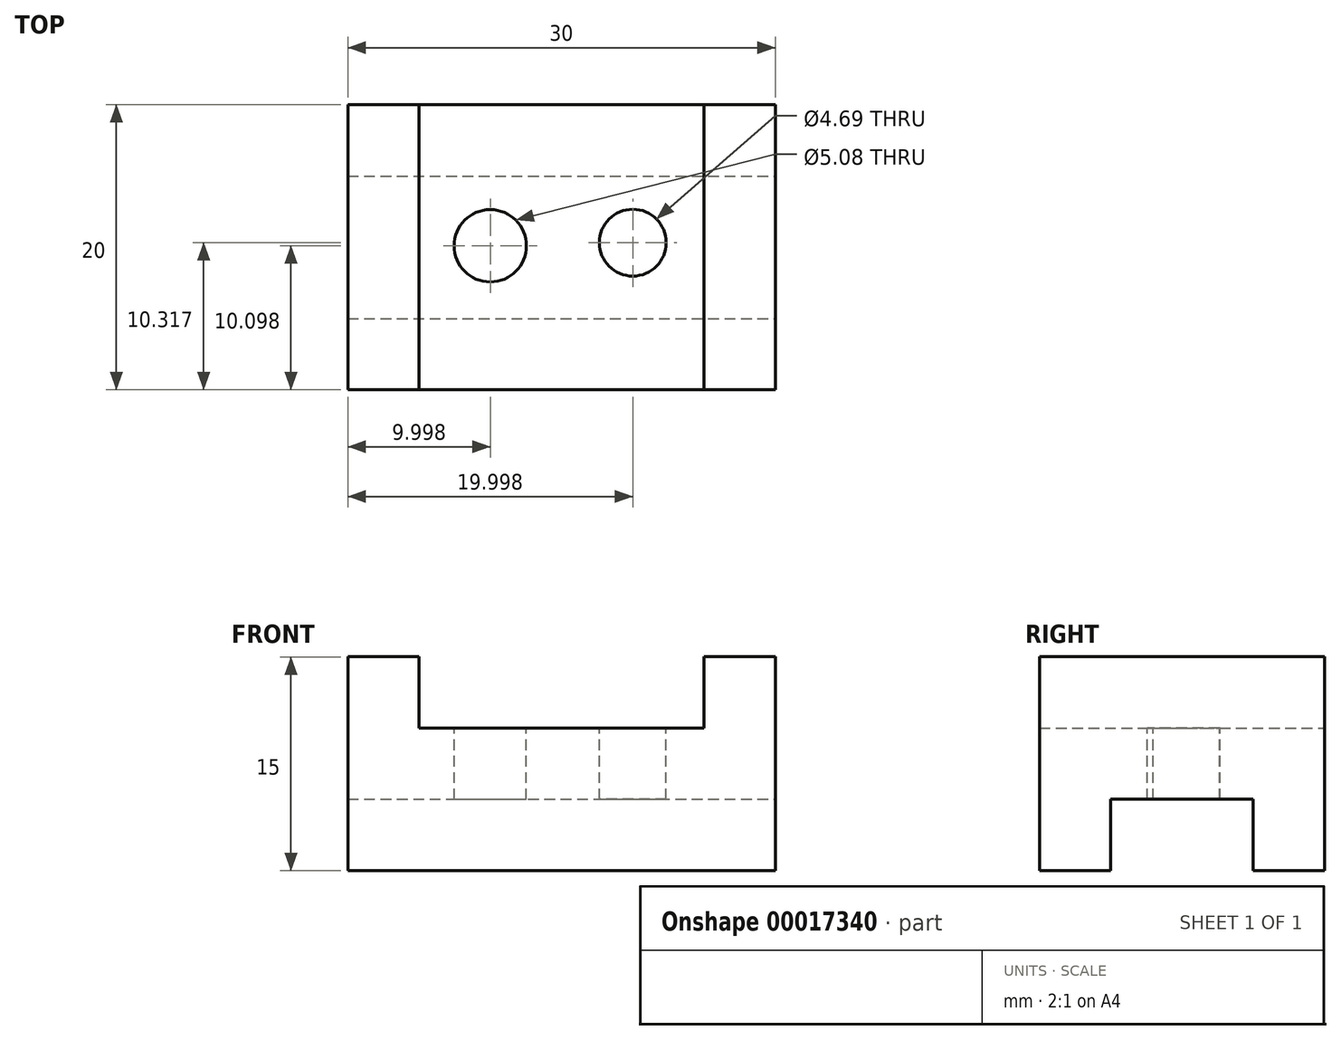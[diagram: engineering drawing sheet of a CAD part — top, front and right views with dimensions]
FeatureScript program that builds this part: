
annotation { "Feature Type Name" : "Feature", "Feature Type Description" : "" }
export const myFeature = defineFeature(function(context is Context, id is Id, definition is map)
    precondition{}
    {
        {
            var Q0;
            Q0=qCreatedBy(makeId("Front.planeOp"),FACE);
            var sketch = newSketch(context, id + "F0", { "sketchPlane" : qUnion([Q0])});
            skLineSegment(sketch, "E0", {"start": v(-14.7, -8.15) * mm, "end": v(-14.7, 6.85) * mm});
            skLineSegment(sketch, "E1", {"start": v(-14.7, 6.85) * mm, "end": v(-9.7, 6.85) * mm});
            skLineSegment(sketch, "E2", {"start": v(-9.7, 6.85) * mm, "end": v(-9.7, 1.85) * mm});
            skLineSegment(sketch, "E3", {"start": v(-9.7, 1.85) * mm, "end": v(10.3, 1.85) * mm});
            skLineSegment(sketch, "E4", {"start": v(10.3, 1.85) * mm, "end": v(10.3, 6.85) * mm});
            skLineSegment(sketch, "E5", {"start": v(10.3, 6.85) * mm, "end": v(15.3, 6.85) * mm});
            skLineSegment(sketch, "E6", {"start": v(15.3, 6.85) * mm, "end": v(15.3, -8.15) * mm});
            skLineSegment(sketch, "E7", {"start": v(15.3, -8.15) * mm, "end": v(-14.7, -8.15) * mm});
            skSolve(sketch);
        }
        {
            var Q0;
            Q0=makeQuery(id+"F0.imprint","IMPRINT",FACE,{"disambiguationData":[TD([[makeQuery(id+"F0.imprint","IMPRINT",EDGE,{"derivedFrom":sQuery(id+"F0.wireOp",EDGE,"E0")}),-1.0]])]});
            extrude(context, id + "F1", {"entities" : qUnion([Q0]), "depth" : 20 * mm});
        }
        {
            var Q0;
            Q0=makeQuery(id+"F1.opExtrude","SWEPT_FACE",FACE,{"disambiguationData":[OSD([sQuery(id+"F0.wireOp",EDGE,"E6")])]});
            var sketch = newSketch(context, id + "F2", { "sketchPlane" : qUnion([Q0])});
            skLineSegment(sketch, "E8", {"start": v(-15, -8.15) * mm, "end": v(-15, -3.15) * mm});
            skLineSegment(sketch, "E9", {"start": v(-15, -3.15) * mm, "end": v(-5, -3.15) * mm});
            skLineSegment(sketch, "E10", {"start": v(-5, -3.15) * mm, "end": v(-5, -8.15) * mm});
            skLineSegment(sketch, "E11", {"start": v(-15, -8.15) * mm, "end": v(-5, -8.15) * mm});
            skSolve(sketch);
        }
        {
            var Q0;
            Q0=makeQuery(id+"F2.imprint","IMPRINT",FACE,{"disambiguationData":[TD([[makeQuery(id+"F2.imprint","IMPRINT",EDGE,{"derivedFrom":sQuery(id+"F2.wireOp",EDGE,"E8")}),-1.0]])]});
            extrude(context, id + "F3", {"entities" : qUnion([Q0]), "operationType" : NewBodyOperationType.REMOVE, "oppositeDirection" : true, "depth" : 50 * mm});
        }
        {
            var Q0;
            Q0=makeQuery(id+"F1.opExtrude","SWEPT_FACE",FACE,{"disambiguationData":[OSD([sQuery(id+"F0.wireOp",EDGE,"E3")])]});
            var sketch = newSketch(context, id + "F4", { "sketchPlane" : qUnion([Q0])});
            skCircle(sketch, "E12", {"center": v(-4.7, -9.9) * mm, "radius": 2.54 * mm});
            skCircle(sketch, "E13", {"center": v(5.3, -9.68) * mm, "radius": 2.34 * mm});
            skSolve(sketch);
        }
        {
            var Q0;
            Q0=makeQuery(id+"F4.imprint","IMPRINT",FACE,{"disambiguationData":[TD([[makeQuery(id+"F4.imprint","IMPRINT",EDGE,{"derivedFrom":sQuery(id+"F4.wireOp",EDGE,"E12")}),1.0]])]});
            var Q1;
            Q1=makeQuery(id+"F4.imprint","IMPRINT",FACE,{"disambiguationData":[TD([[makeQuery(id+"F4.imprint","IMPRINT",EDGE,{"derivedFrom":sQuery(id+"F4.wireOp",EDGE,"E13")}),1.0]])]});
            extrude(context, id + "F5", {"entities" : qUnion([Q0, Q1]), "operationType" : NewBodyOperationType.REMOVE, "oppositeDirection" : true, "depth" : 25 * mm});
        }
    });
